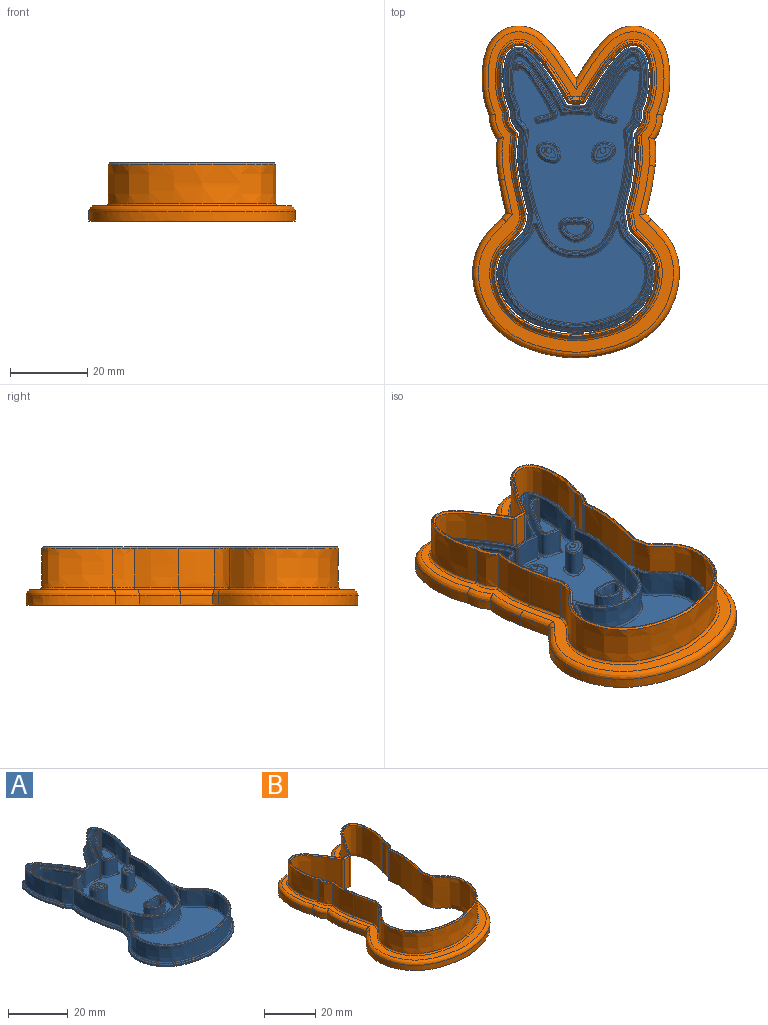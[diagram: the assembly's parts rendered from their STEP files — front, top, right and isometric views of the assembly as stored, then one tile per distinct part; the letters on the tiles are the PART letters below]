
ASSEMBLY  parts=2 mates=1
PART A: 215 faces, bbox 40.7x74.1x8.3 mm
  f0: plane 50.26x32.65mm, normal (0,0,1), area 800.4mm2, adj f99,f102,f103,f104,f105,f106,f108,f109
  f1: plane 72.95x39.59mm, normal (0,0,1), area 46mm2, adj f87,f88,f89,f90,f91,f92,f93,f94
  f2: extruded ~40.37x31.14mm, area 55.5mm2, adj f8,f81,f84,f93
  f3: extruded ~20.21x2.63mm, area 12.3mm2, adj f8,f81,f82,f89
  f4: extruded ~22.02x16.22mm, area 26.9mm2, adj f8,f82,f83,f88
  f5: extruded ~4.36x0.6mm, area 2.6mm2, adj f8,f83,f85,f92
  f6: extruded ~22.03x16.23mm, area 26.9mm2, adj f8,f85,f86,f96
  f7: extruded ~20.61x2.74mm, area 12.5mm2, adj f8,f84,f86,f97
  f8: plane 73.75x40.39mm, normal (0,0,-1), area 2157.8mm2, adj f2,f3,f4,f5,f6,f7,f81,f82
  f9: extruded ~20.77x6.3mm, area 132.8mm2, adj f69,f80,f154,f184
  f10: extruded ~6.3x2.39mm, area 15.2mm2, adj f11,f80,f150,f181
  f11: extruded ~38.28x28.27mm, area 536.7mm2, adj f10,f12,f148,f183
  f12: extruded ~6.3x1.83mm, area 11.8mm2, adj f11,f73,f146,f185
  f13: extruded ~20.52x6.3mm, area 131.2mm2, adj f72,f73,f142,f189
  f14: extruded ~20.72x14.29mm, area 263.6mm2, adj f15,f72,f139,f193
  f15: extruded ~6.3x0.73mm, area 5mm2, adj f14,f71,f141,f195
  f16: extruded ~6.3x0.78mm, area 4.9mm2, adj f17,f71,f145,f198
  f17: extruded ~6.3x4.03mm, area 25.5mm2, adj f16,f18,f147,f196
  f18: extruded ~6.3x0.78mm, area 4.9mm2, adj f17,f70,f149,f194
  f19: extruded ~6.3x0.73mm, area 5mm2, adj f30,f70,f153,f190
  f20: extruded ~20.95x6.3mm, area 134mm2, adj f21,f75,f125,f214
  f21: extruded ~20.72x10.43mm, area 203.8mm2, adj f20,f22,f129,f212
  f22: extruded ~20.95x6.3mm, area 134mm2, adj f21,f78,f131,f210
  f23: extruded ~19.44x12.93mm, area 253.6mm2, adj f77,f78,f130,f206
  f24: extruded ~6.92x6.3mm, area 43.9mm2, adj f76,f77,f122,f207
  f25: extruded ~36.38x25.18mm, area 494.2mm2, adj f26,f29,f134,f202
  f26: extruded ~6.3x0.7mm, area 4.6mm2, adj f25,f79,f133,f200
  f27: extruded ~20.73x8.45mm, area 181mm2, adj f74,f79,f137,f201
  f28: extruded ~19.43x12.93mm, area 253.6mm2, adj f75,f76,f117,f211
  f29: extruded ~6.3x0.9mm, area 5.8mm2, adj f25,f74,f136,f204
  f30: extruded ~20.72x14.29mm, area 263.6mm2, adj f19,f69,f155,f188
  f31: plane 71.65x38.23mm, normal (0,0,1), area 105.7mm2, adj f181,f182,f183,f184,f185,f186,f187,f188
  f32: plane 35.59x25.24mm, normal (0,0,1), area 586.4mm2, adj f133,f134,f136,f137
  f33: extruded ~7x0.04mm, area 0.4mm2, adj f34,f36,f38,f39
  f34: extruded ~7x3.51mm, area 64.8mm2, adj f33,f35,f38,f39
  f35: extruded ~7x0.06mm, area 0.7mm2, adj f34,f36,f38,f39
  f36: cylinder r=0.74mm len=7mm, axis (0,0,-1), area 27.3mm2, adj f33,f35,f38,f39
  f37: extruded ~6.3x5.51mm, area 223.8mm2, adj f160,f162
  f38: plane 5.28x4.45mm, normal (0,0,1), area 10mm2, adj f33,f34,f35,f36,f162
  f39: plane 3.57x2.76mm, normal (0,0,1), area 5.3mm2, adj f33,f34,f35,f36
  f40: extruded ~7x0.06mm, area 0.7mm2, adj f41,f43,f45,f46
  f41: cylinder r=0.74mm len=7mm, axis (0,0,-1), area 26.6mm2, adj f40,f42,f45,f46
  f42: extruded ~7x0.09mm, area 0.8mm2, adj f41,f43,f45,f46
  f43: extruded ~7x3.51mm, area 64.1mm2, adj f40,f42,f45,f46
  f44: extruded ~6.3x5.51mm, area 223.8mm2, adj f159,f161
  f45: plane 5.28x4.44mm, normal (0,0,1), area 10.1mm2, adj f40,f41,f42,f43,f161
  f46: plane 3.57x2.76mm, normal (0,0,1), area 5.2mm2, adj f40,f41,f42,f43
  f47: extruded ~6.3x6.27mm, area 101.8mm2, adj f158,f180
  f48: extruded ~8.26x6.3mm, area 140.7mm2, adj f157,f179
  f49: plane 7.97x5.31mm, normal (0,0,1), area 7.6mm2, adj f179,f180
  f50: plane 5.48x2.91mm, normal (0,0,1), area 12.1mm2, adj f158
  f51: plane 6.3x0.35mm, normal (0.87,-0.5,0), area 2.5mm2, adj f62,f63,f106,f165
  f52: extruded ~13.33x8.85mm, area 124.1mm2, adj f63,f64,f99,f100,f101,f102,f103,f164
  f53: plane 6.3x0.41mm, normal (0.1,-1,0), area 2.6mm2, adj f61,f64,f109,f168
  f54: extruded ~15.21x10.82mm, area 149.5mm2, adj f61,f62,f114,f169
  f55: plane 14.71x10.25mm, normal (0,0,1), area 8.9mm2, adj f164,f165,f168,f169
  f56: extruded ~13.33x8.85mm, area 124.1mm2, adj f65,f66,f107,f108,f111,f112,f116,f173
  f57: plane 6.3x0.35mm, normal (-0.87,-0.5,0), area 2.5mm2, adj f65,f68,f119,f172
  f58: extruded ~15.21x10.82mm, area 149.5mm2, adj f67,f68,f127,f176
  f59: plane 6.3x0.41mm, normal (-0.1,-1,0), area 2.6mm2, adj f66,f67,f124,f177
  f60: plane 14.71x10.25mm, normal (0,0,1), area 9.1mm2, adj f172,f173,f176,f177
  f61: cylinder r=0.3mm len=6.3mm, axis (0,0,-1), area 3.3mm2, adj f53,f54,f113,f170
  f62: cylinder r=0.3mm len=6.3mm, axis (0,0,-1), area 2.8mm2, adj f51,f54,f110,f167
  f63: cylinder r=0.3mm len=6.3mm, axis (0,0,-1), area 3.1mm2, adj f51,f52,f104,f163
  f64: cylinder r=0.3mm len=6.3mm, axis (0,0,-1), area 2.5mm2, adj f52,f53,f105,f166
  f65: cylinder r=0.3mm len=6.3mm, axis (0,0,-1), area 3.1mm2, adj f56,f57,f115,f171
  f66: cylinder r=0.3mm len=6.3mm, axis (0,0,-1), area 2.5mm2, adj f56,f59,f120,f175
  f67: cylinder r=0.3mm len=6.3mm, axis (0,0,-1), area 3.3mm2, adj f58,f59,f128,f178
  f68: cylinder r=0.3mm len=6.3mm, axis (0,0,-1), area 2.8mm2, adj f57,f58,f123,f174
  f69: cylinder r=0.3mm len=6.3mm, axis (0,0,-1), area 1.3mm2, adj f9,f30,f156,f186
  f70: cylinder r=0.3mm len=6.3mm, axis (0,0,-1), area 2.5mm2, adj f18,f19,f151,f192
  f71: cylinder r=0.3mm len=6.3mm, axis (0,0,-1), area 2.5mm2, adj f15,f16,f143,f197
  f72: cylinder r=0.3mm len=6.3mm, axis (0,0,-1), area 1.3mm2, adj f13,f14,f140,f191
  f73: cylinder r=0.3mm len=6.3mm, axis (0,0,-1), area 1.2mm2, adj f12,f13,f144,f187
  f74: cylinder r=0.3mm len=6.3mm, axis (0,0,-1), area 5.1mm2, adj f27,f29,f138,f203
  f75: cylinder r=0.3mm len=6.3mm, axis (0,0,-1), area 1.2mm2, adj f20,f28,f121,f213
  f76: cylinder r=0.3mm len=6.3mm, axis (0,0,-1), area 2.7mm2, adj f24,f28,f118,f209
  f77: cylinder r=0.3mm len=6.3mm, axis (0,0,-1), area 2.7mm2, adj f23,f24,f126,f205
  f78: cylinder r=0.3mm len=6.3mm, axis (0,0,-1), area 1.2mm2, adj f22,f23,f132,f208
  f79: cylinder r=0.3mm len=6.3mm, axis (0,0,-1), area 4.7mm2, adj f26,f27,f135,f199
  f80: cylinder r=0.3mm len=6.3mm, axis (0,0,-1), area 0.6mm2, adj f9,f10,f152,f182
  f81: cylinder r=0.3mm len=0.6mm, axis (0,0,-1), area 0.1mm2, adj f2,f3,f8,f91
  f82: cylinder r=0.3mm len=0.6mm, axis (0,0,-1), area 0.1mm2, adj f3,f4,f8,f87
  f83: cylinder r=0.3mm len=0.6mm, axis (0,0,-1), area 0.2mm2, adj f4,f5,f8,f90
  f84: cylinder r=0.3mm len=0.6mm, axis (0,0,-1), area 0.1mm2, adj f2,f7,f8,f95
  f85: cylinder r=0.3mm len=0.6mm, axis (0,0,-1), area 0.2mm2, adj f5,f6,f8,f94
  f86: cylinder r=0.3mm len=0.6mm, axis (0,0,-1), area 0.1mm2, adj f6,f7,f8,f98
  f87: torus R=0.7mm, axis (0,0,1), area 0.2mm2, adj f1,f82,f88,f89
  f88: bspline ~22.34x16.45mm, area 27.8mm2, adj f1,f4,f87,f90
  f89: bspline ~23.91x3.7mm, area 12.8mm2, adj f1,f3,f87,f91
  f90: torus R=0.7mm, axis (0,0,1), area 0.4mm2, adj f1,f83,f88,f92
  f91: torus R=0.7mm, axis (0,0,1), area 0.2mm2, adj f1,f81,f89,f93
  f92: bspline ~6.28x0.7mm, area 2.7mm2, adj f1,f5,f90,f94
  f93: bspline ~40.39x31.62mm, area 57.8mm2, adj f1,f2,f91,f95
  f94: torus R=0.7mm, axis (0,0,1), area 0.4mm2, adj f1,f85,f92,f96
  f95: torus R=0.7mm, axis (0,0,1), area 0.1mm2, adj f1,f84,f93,f97
  f96: bspline ~22.35x16.45mm, area 27.7mm2, adj f1,f6,f94,f98
  f97: bspline ~26.44x4.46mm, area 13.1mm2, adj f1,f7,f95,f98
  f98: torus R=0.7mm, axis (0,0,1), area 0.2mm2, adj f1,f86,f96,f97
  f99: bspline ~12.02x8.65mm, area 9.3mm2, adj f0,f52,f100,f101
  f100: bspline ~0.41x0.4mm, area 0.1mm2, adj f52,f99,f102
  f101: bspline ~0.4x0.39mm, area 0.1mm2, adj f52,f99,f103
  f102: bspline ~4.25x1.65mm, area 2.4mm2, adj f0,f52,f100,f104
  f103: bspline ~0.42x0.4mm, area 0mm2, adj f0,f52,f101,f105
  f104: torus R=0.7mm, axis (0,0,1), area 0.5mm2, adj f0,f63,f102,f106
  f105: torus R=0.7mm, axis (0,0,1), area 0.4mm2, adj f0,f64,f103,f109
  f106: cylinder r=0.4mm len=0.55mm, axis (-0.5,-0.87,0), area 0.3mm2, adj f0,f51,f104,f110
  f107: bspline ~0.41x0.4mm, area 0.1mm2, adj f56,f108,f111
  f108: bspline ~12.03x8.68mm, area 9.3mm2, adj f0,f56,f107,f112
  f109: cylinder r=0.4mm len=0.45mm, axis (-1,-0.1,0), area 0.3mm2, adj f0,f53,f105,f113
  f110: torus R=0.7mm, axis (0,0,1), area 0.4mm2, adj f0,f62,f106,f114
  f111: bspline ~4.17x1.61mm, area 2.4mm2, adj f0,f56,f107,f115
  f112: bspline ~0.4x0.39mm, area 0.1mm2, adj f56,f108,f116
  f113: torus R=0.7mm, axis (0,0,1), area 0.4mm2, adj f0,f61,f109,f114,f117
  f114: bspline ~16.12x11.68mm, area 15.2mm2, adj f0,f54,f110,f113,f117
  f115: torus R=0.7mm, axis (0,0,1), area 0.5mm2, adj f0,f65,f111,f119
  f116: bspline ~0.42x0.4mm, area 0mm2, adj f0,f56,f112,f120
  f117: bspline ~19.63x12.96mm, area 24.8mm2, adj f0,f28,f113,f114,f118,f121
  f118: torus R=0.7mm, axis (0,0,1), area 0.4mm2, adj f0,f76,f117,f122
  f119: cylinder r=0.4mm len=0.55mm, axis (-0.5,0.87,0), area 0.3mm2, adj f0,f57,f115,f123
  f120: torus R=0.7mm, axis (0,0,1), area 0.4mm2, adj f0,f66,f116,f124
  f121: torus R=0.7mm, axis (0,0,1), area 0.2mm2, adj f0,f75,f117,f125
  f122: bspline ~10.8x1.05mm, area 4.3mm2, adj f0,f24,f118,f126
  f123: torus R=0.7mm, axis (0,0,1), area 0.4mm2, adj f0,f68,f119,f127
  f124: cylinder r=0.4mm len=0.45mm, axis (-1,0.1,0), area 0.3mm2, adj f0,f59,f120,f128
  f125: bspline ~25.61x4.43mm, area 13.3mm2, adj f0,f20,f121,f129
  f126: torus R=0.7mm, axis (0,0,1), area 0.4mm2, adj f0,f77,f122,f130
  f127: bspline ~16.12x11.68mm, area 15.2mm2, adj f0,f58,f123,f128,f130
  f128: torus R=0.7mm, axis (0,0,1), area 0.4mm2, adj f0,f67,f124,f127,f130
  f129: bspline ~23.98x16.12mm, area 20.1mm2, adj f0,f21,f125,f131
  f130: bspline ~20.07x13.03mm, area 24.8mm2, adj f0,f23,f126,f127,f128,f132
  f131: bspline ~25.73x4.46mm, area 13.3mm2, adj f0,f22,f129,f132
  f132: torus R=0.7mm, axis (0,0,1), area 0.2mm2, adj f0,f78,f130,f131
  f133: bspline ~1.26x0.75mm, area 0.4mm2, adj f26,f32,f134,f135
  f134: bspline ~36.87x36.39mm, area 48.9mm2, adj f25,f32,f133,f136
  f135: bspline ~1.28x0.62mm, area 0.3mm2, adj f79,f133,f137
  f136: bspline ~1.53x0.62mm, area 0.4mm2, adj f29,f32,f134,f138
  f137: bspline ~23.48x13.79mm, area 18.1mm2, adj f27,f32,f135,f138
  f138: bspline ~1.71x0.89mm, area 0.3mm2, adj f74,f136,f137
  f139: bspline ~30.12x22.24mm, area 26.5mm2, adj f1,f14,f140,f141
  f140: bspline ~0.49x0.41mm, area 0.1mm2, adj f72,f139,f142
  f141: bspline ~1.2x0.82mm, area 0.5mm2, adj f1,f15,f139,f143
  f142: bspline ~22.36x3.34mm, area 13.1mm2, adj f1,f13,f140,f144
  f143: bspline ~0.51x0.44mm, area 0.1mm2, adj f71,f141,f145
  f144: bspline ~0.49x0.42mm, area 0mm2, adj f73,f142,f146
  f145: bspline ~1.18x0.55mm, area 0.5mm2, adj f1,f16,f143,f147
  f146: bspline ~2.65x0.98mm, area 1.2mm2, adj f1,f12,f144,f148
  f147: bspline ~10.83x1.4mm, area 2.6mm2, adj f1,f17,f145,f149
  f148: bspline ~40.14x39.18mm, area 53.9mm2, adj f1,f11,f146,f150
  f149: bspline ~1.18x0.55mm, area 0.5mm2, adj f1,f18,f147,f151
  f150: bspline ~3.59x0.81mm, area 1.5mm2, adj f1,f10,f148,f152
  f151: bspline ~0.51x0.44mm, area 0.1mm2, adj f70,f149,f153
  f152: bspline ~0.49x0.4mm, area 0mm2, adj f80,f150,f154
  f153: bspline ~1.2x0.82mm, area 0.5mm2, adj f1,f19,f151,f155
  f154: bspline ~25.46x3.41mm, area 13.3mm2, adj f1,f9,f152,f156
  f155: bspline ~30.12x22.24mm, area 26.4mm2, adj f1,f30,f153,f156
  f156: bspline ~0.49x0.41mm, area 0.1mm2, adj f69,f154,f155
  f157: bspline ~9.09x6.51mm, area 14.7mm2, adj f0,f48
  f158: bspline ~6.28x3.71mm, area 9.5mm2, adj f47,f50
  f159: bspline ~6.31x5.52mm, area 10.8mm2, adj f0,f44
  f160: bspline ~6.32x5.52mm, area 21.6mm2, adj f0,f37
  f161: bspline ~5.58x4.76mm, area 6.5mm2, adj f44,f45
  f162: bspline ~5.58x4.75mm, area 6.5mm2, adj f37,f38
  f163: cone r=0.3mm half-angle=45deg, axis (0,0,-1), area 0.1mm2, adj f63,f164,f165
  f164: bspline ~13.94x9.44mm, area 8.6mm2, adj f52,f55,f163,f166
  f165: plane 0.5x0.46mm, normal (0.61,-0.35,0.71), area 0.2mm2, adj f51,f55,f163,f167
  f166: cone r=0.3mm half-angle=45deg, axis (0,0,-1), area 0.1mm2, adj f64,f164,f168
  f167: cone r=0.3mm half-angle=45deg, axis (0,0,-1), area 0.1mm2, adj f62,f165,f169
  f168: plane 0.44x0.34mm, normal (0.07,-0.7,0.71), area 0.2mm2, adj f53,f55,f166,f170
  f169: bspline ~15.25x10.83mm, area 9.8mm2, adj f54,f55,f167,f170
  f170: cone r=0.3mm half-angle=45deg, axis (0,0,-1), area 0.2mm2, adj f61,f168,f169
  f171: cone r=0.3mm half-angle=45deg, axis (0,0,-1), area 0.1mm2, adj f65,f172,f173
  f172: plane 0.58x0.54mm, normal (-0.61,-0.35,0.71), area 0.2mm2, adj f57,f60,f171,f174
  f173: bspline ~13.94x9.44mm, area 8.6mm2, adj f56,f60,f171,f175
  f174: cone r=0.3mm half-angle=45deg, axis (0,0,-1), area 0.1mm2, adj f68,f172,f176
  f175: cone r=0.3mm half-angle=45deg, axis (0,0,-1), area 0.1mm2, adj f66,f173,f177
  f176: bspline ~15.25x10.83mm, area 9.8mm2, adj f58,f60,f174,f178
  f177: plane 0.69x0.59mm, normal (-0.07,-0.7,0.71), area 0.2mm2, adj f59,f60,f175,f178
  f178: cone r=0.3mm half-angle=45deg, axis (0,0,-1), area 0.1mm2, adj f67,f176,f177
  f179: bspline ~8.26x5.7mm, area 9.1mm2, adj f48,f49
  f180: bspline ~6.97x4.31mm, area 7.3mm2, adj f47,f49
  f181: bspline ~2.46x0.59mm, area 1mm2, adj f10,f31,f182,f183
  f182: cone r=0.6mm half-angle=45deg, axis (0,0,1), area 0.1mm2, adj f31,f80,f181,f184
  f183: bspline ~38.44x28.3mm, area 35.9mm2, adj f11,f31,f181,f185
  f184: bspline ~20.77x3.05mm, area 8.9mm2, adj f9,f31,f182,f186
  f185: bspline ~1.87x0.71mm, area 0.8mm2, adj f12,f31,f183,f187
  f186: cone r=0.6mm half-angle=45deg, axis (0,0,1), area 0.1mm2, adj f31,f69,f184,f188
  f187: cone r=0.6mm half-angle=45deg, axis (0,0,1), area 0.1mm2, adj f31,f73,f185,f189
  f188: bspline ~20.8x14.31mm, area 17.4mm2, adj f30,f31,f186,f190
  f189: bspline ~20.52x2.98mm, area 8.8mm2, adj f13,f31,f187,f191
  f190: bspline ~0.84x0.59mm, area 0.3mm2, adj f19,f31,f188,f192
  f191: cone r=0.6mm half-angle=45deg, axis (0,0,1), area 0.1mm2, adj f31,f72,f189,f193
  f192: cone r=0.6mm half-angle=45deg, axis (0,0,1), area 0.3mm2, adj f31,f70,f190,f194
  f193: bspline ~20.8x14.31mm, area 17.4mm2, adj f14,f31,f191,f195
  f194: bspline ~0.82x0.4mm, area 0.3mm2, adj f18,f31,f192,f196
  f195: bspline ~0.84x0.59mm, area 0.3mm2, adj f15,f31,f193,f197
  f196: bspline ~4.03x0.45mm, area 1.7mm2, adj f17,f31,f194,f198
  f197: cone r=0.6mm half-angle=45deg, axis (0,0,1), area 0.3mm2, adj f31,f71,f195,f198
  f198: bspline ~0.82x0.4mm, area 0.3mm2, adj f16,f31,f196,f197
  f199: cone r=0.6mm half-angle=45deg, axis (0,0,1), area 0.5mm2, adj f31,f79,f200,f201
  f200: bspline ~0.78x0.51mm, area 0.3mm2, adj f26,f31,f199,f202
  f201: bspline ~20.73x8.58mm, area 12mm2, adj f27,f31,f199,f203
  f202: bspline ~37.05x25.54mm, area 33.6mm2, adj f25,f31,f200,f204
  f203: cone r=0.6mm half-angle=45deg, axis (0,0,1), area 0.5mm2, adj f31,f74,f201,f204
  f204: bspline ~0.94x0.43mm, area 0.4mm2, adj f29,f31,f202,f203
  f205: cone r=0.3mm half-angle=45deg, axis (0,0,-1), area 0.1mm2, adj f77,f206,f207
  f206: bspline ~19.97x13.54mm, area 17.3mm2, adj f23,f31,f205,f208
  f207: bspline ~7.01x0.67mm, area 3mm2, adj f24,f31,f205,f209
  f208: cone r=0.3mm half-angle=45deg, axis (0,0,-1), area 0mm2, adj f78,f206,f210
  f209: cone r=0.3mm half-angle=45deg, axis (0,0,-1), area 0.1mm2, adj f76,f207,f211
  f210: bspline ~21.06x3.08mm, area 9mm2, adj f22,f31,f208,f212
  f211: bspline ~19.97x13.54mm, area 17.3mm2, adj f28,f31,f209,f213
  f212: bspline ~21.3x10.73mm, area 13.9mm2, adj f21,f31,f210,f214
  f213: cone r=0.3mm half-angle=45deg, axis (0,0,-1), area 0mm2, adj f75,f211,f214
  f214: bspline ~21.06x3.08mm, area 9mm2, adj f20,f31,f212,f213
PART B: 91 faces, bbox 53.8x86.1x15.4 mm
  f0: plane 82.75x50.39mm, normal (0,0,1), area 572.8mm2, adj f58,f59,f60,f61,f62,f63,f64,f65
  f1: extruded ~10x0.82mm, area 9.4mm2, adj f13,f40,f78,f83
  f2: extruded ~10x0.82mm, area 9.4mm2, adj f3,f36,f82,f85
  f3: extruded ~18.28x17.96mm, area 406.9mm2, adj f2,f4,f37,f81
  f4: extruded ~10x5.71mm, area 63.3mm2, adj f3,f5,f39,f79
  f5: extruded ~10x8.17mm, area 82.1mm2, adj f4,f6,f41,f77
  f6: extruded ~11.79x10mm, area 120.3mm2, adj f5,f7,f43,f75
  f7: extruded ~10x4.88mm, area 51.1mm2, adj f6,f8,f45,f73
  f8: extruded ~43.32x28.27mm, area 879.8mm2, adj f7,f9,f47,f71
  f9: extruded ~10x3.9mm, area 41.5mm2, adj f8,f10,f49,f69
  f10: extruded ~10x9.31mm, area 95.4mm2, adj f9,f11,f48,f70
  f11: extruded ~11.2x10mm, area 112.6mm2, adj f10,f12,f46,f72
  f12: extruded ~10x5.72mm, area 63.5mm2, adj f11,f13,f44,f74
  f13: extruded ~18.28x17.96mm, area 406.9mm2, adj f1,f12,f42,f76
  f14: extruded ~20.29x14.6mm, area 300.8mm2, adj f15,f24,f52,f87
  f15: extruded ~41.37x31.73mm, area 1374.9mm2, adj f14,f16,f24,f54
  f16: extruded ~19.86x14.6mm, area 294.2mm2, adj f15,f24,f56,f90
  f17: extruded ~14.6x5.27mm, area 85.3mm2, adj f18,f24,f57,f90
  f18: extruded ~17.16x16.82mm, area 568.5mm2, adj f17,f24,f55,f88
  f19: extruded ~14.6x2.82mm, area 41.2mm2, adj f24,f53,f88,f89
  f20: extruded ~17.18x16.82mm, area 570.6mm2, adj f22,f24,f51,f89
  f21: extruded ~10x1.73mm, area 17.3mm2, adj f38,f80,f83,f85
  f22: extruded ~14.6x5.26mm, area 85mm2, adj f20,f24,f50,f87
  f23: plane 76.77x43.03mm, normal (0,0,1), area 36.4mm2, adj f36,f37,f38,f39,f40,f41,f42,f43
  f24: plane 85.75x53.38mm, normal (0,0,-1), area 1344.2mm2, adj f14,f15,f16,f17,f18,f19,f20,f22
  f25: plane 2.5x1.32mm, normal (-0.77,0.63,0), area 4.3mm2, adj f24,f26,f35,f64
  f26: extruded ~8.43x2.5mm, area 21.6mm2, adj f24,f25,f27,f62
  f27: extruded ~10.62x2.5mm, area 26.7mm2, adj f24,f26,f28,f60
  f28: extruded ~6.15x2.5mm, area 16.5mm2, adj f24,f27,f29,f58
  f29: extruded ~24.22x23.01mm, area 123.7mm2, adj f24,f28,f30,f59
  f30: extruded ~24.22x23.01mm, area 123.7mm2, adj f24,f29,f31,f61
  f31: extruded ~6.14x2.5mm, area 16.5mm2, adj f24,f30,f32,f63
  f32: extruded ~7.01x2.5mm, area 17.6mm2, adj f24,f31,f33,f65
  f33: extruded ~12.2x2.5mm, area 31.1mm2, adj f24,f32,f34,f67
  f34: plane 2.5x1.51mm, normal (0.74,0.67,0), area 5.1mm2, adj f24,f33,f35,f68
  f35: extruded ~53.37x36.13mm, area 274mm2, adj f24,f25,f34,f66
  f36: bspline ~2x1.42mm, area 1.1mm2, adj f2,f23,f37,f38,f85
  f37: bspline ~18.6x17.98mm, area 22.6mm2, adj f3,f23,f36,f39
  f38: bspline ~3.94x0.69mm, area 2mm2, adj f21,f23,f36,f40,f83,f85
  f39: bspline ~6.32x2.86mm, area 3.6mm2, adj f4,f23,f37,f41
  f40: bspline ~2x1.42mm, area 1.1mm2, adj f1,f23,f38,f42,f83
  f41: bspline ~8.33x0.88mm, area 4.7mm2, adj f5,f23,f39,f43
  f42: bspline ~18.6x17.98mm, area 22.6mm2, adj f13,f23,f40,f44
  f43: bspline ~11.93x2.79mm, area 6.8mm2, adj f6,f23,f41,f45
  f44: bspline ~6.33x2.87mm, area 3.6mm2, adj f12,f23,f42,f46
  f45: bspline ~5.51x1.77mm, area 3mm2, adj f7,f23,f43,f47
  f46: bspline ~11.92x1.07mm, area 6.4mm2, adj f11,f23,f44,f48
  f47: bspline ~43.42x28.29mm, area 49.4mm2, adj f8,f23,f45,f49
  f48: bspline ~9.43x2.49mm, area 5.4mm2, adj f10,f23,f46,f49
  f49: bspline ~4.43x1.63mm, area 2.4mm2, adj f9,f23,f47,f48
  f50: bspline ~6.07x2.88mm, area 3.5mm2, adj f22,f23,f51,f52,f87
  f51: bspline ~18.77x17.72mm, area 22.7mm2, adj f20,f23,f50,f53,f89
  f52: bspline ~22.9x3.46mm, area 11.8mm2, adj f14,f23,f50,f54,f87
  f53: bspline ~4.72x0.58mm, area 2.1mm2, adj f19,f23,f51,f55,f88,f89
  f54: bspline ~42.24x34.72mm, area 53.6mm2, adj f15,f23,f52,f56
  f55: bspline ~18.77x17.71mm, area 22.7mm2, adj f18,f23,f53,f57,f88
  f56: bspline ~22.44x3.32mm, area 11.6mm2, adj f16,f23,f54,f57,f90
  f57: bspline ~5.81x2.67mm, area 3.5mm2, adj f17,f23,f55,f56,f90
  f58: bspline ~8.58x4.65mm, area 15.8mm2, adj f0,f28,f59,f60
  f59: bspline ~26.3x23.57mm, area 115.4mm2, adj f0,f29,f58,f61
  f60: bspline ~14.78x2.63mm, area 25.5mm2, adj f0,f27,f58,f62
  f61: bspline ~26.3x23.59mm, area 115.4mm2, adj f0,f30,f59,f63
  f62: bspline ~12.04x4.11mm, area 21.1mm2, adj f0,f26,f60,f64
  f63: bspline ~9.62x3.76mm, area 15.8mm2, adj f0,f31,f61,f65
  f64: cylinder r=1.5mm len=2.86mm, axis (-0.63,-0.77,0), area 4.9mm2, adj f0,f25,f62,f66
  f65: bspline ~19.11x2.87mm, area 17mm2, adj f0,f32,f63,f67
  f66: bspline ~53.39x36.3mm, area 252.9mm2, adj f0,f35,f64,f68
  f67: bspline ~17.02x4.57mm, area 30.1mm2, adj f0,f33,f65,f68
  f68: cylinder r=1.5mm len=3.16mm, axis (-0.67,0.74,0), area 5.8mm2, adj f0,f34,f66,f67
  f69: bspline ~5.07x2.21mm, area 3.7mm2, adj f0,f9,f70,f71
  f70: bspline ~24.28x5.23mm, area 9mm2, adj f0,f10,f69,f72
  f71: bspline ~44.59x35.51mm, area 83.8mm2, adj f0,f8,f69,f73
  f72: bspline ~14.35x1.69mm, area 10.6mm2, adj f0,f11,f70,f74
  f73: bspline ~6.26x2.64mm, area 4.7mm2, adj f0,f7,f71,f75
  f74: bspline ~6.7x3.02mm, area 6mm2, adj f0,f12,f72,f76
  f75: bspline ~31.33x5.39mm, area 11.3mm2, adj f0,f6,f73,f77
  f76: bspline ~23.01x21.19mm, area 38.7mm2, adj f0,f13,f74,f78
  f77: bspline ~9.25x1.11mm, area 7.7mm2, adj f0,f5,f75,f79
  f78: bspline ~1.58x1.24mm, area 0.9mm2, adj f0,f1,f76,f84
  f79: bspline ~6.39x3.03mm, area 5.9mm2, adj f0,f4,f77,f81
  f80: bspline ~2.48x0.66mm, area 1.7mm2, adj f0,f21,f84,f86
  f81: bspline ~23.01x21.19mm, area 38.7mm2, adj f0,f3,f79,f82
  f82: bspline ~1.58x1.24mm, area 0.9mm2, adj f0,f2,f81,f86
  f83: cylinder r=1mm len=10mm, axis (0,0,-1), area 11.4mm2, adj f1,f21,f38,f40,f84
  f84: torus R=0.4mm, axis (0,0,-1), area 0.8mm2, adj f0,f78,f80,f83
  f85: cylinder r=1mm len=10mm, axis (0,0,-1), area 11.4mm2, adj f2,f21,f36,f38,f86
  f86: torus R=0.4mm, axis (0,0,-1), area 0.8mm2, adj f0,f80,f82,f85
  f87: cylinder r=1mm len=14.67mm, axis (0,0,-1), area 11.1mm2, adj f14,f22,f24,f50,f52
  f88: cylinder r=1mm len=14.78mm, axis (0,0,-1), area 17.7mm2, adj f18,f19,f24,f53,f55
  f89: cylinder r=1mm len=14.78mm, axis (0,0,-1), area 17.7mm2, adj f19,f20,f24,f51,f53
  f90: cylinder r=1mm len=14.67mm, axis (0,0,-1), area 11.2mm2, adj f16,f17,f24,f56,f57
PLACE A t=(-3.62,-56.2,14.69)mm
PLACE B t=(-3.61,-56.27,14.69)mm
MATE fastened A.f8 <-> B.f24  axis (0,0,-1) through (-3.62,13.08,14.69)mm
